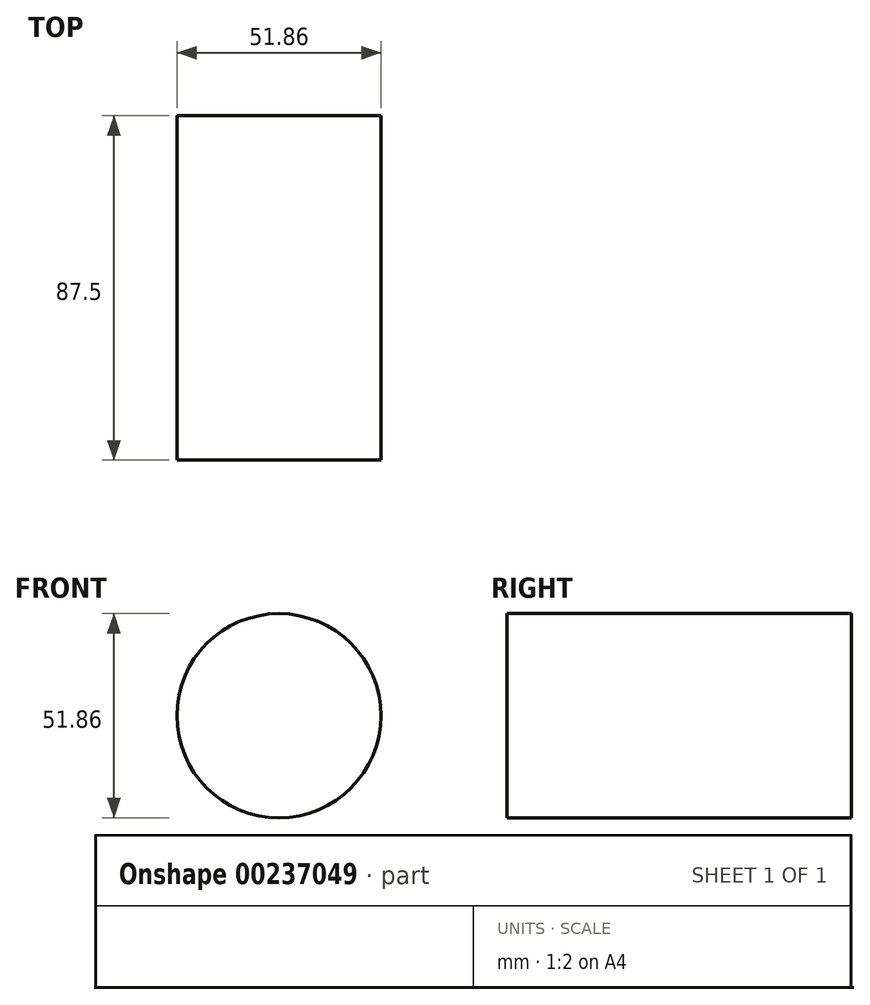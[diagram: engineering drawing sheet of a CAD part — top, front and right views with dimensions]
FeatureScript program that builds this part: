
annotation { "Feature Type Name" : "Feature", "Feature Type Description" : "" }
export const myFeature = defineFeature(function(context is Context, id is Id, definition is map)
    precondition{}
    {
        {
            var Q0;
            Q0=qCreatedBy(makeId("Front.planeOp"),FACE);
            var sketch = newSketch(context, id + "F0", { "sketchPlane" : qUnion([Q0])});
            skCircle(sketch, "E0", {"center": v(-28.26, 35.9) * mm, "radius": 25.93 * mm});
            skSolve(sketch);
        }
        {
            var Q0;
            Q0=makeQuery(id+"F0.imprint","IMPRINT",FACE,{"disambiguationData":[TD([[makeQuery(id+"F0.imprint","IMPRINT",EDGE,{"derivedFrom":sQuery(id+"F0.wireOp",EDGE,"E0")}),1.0]])]});
            extrude(context, id + "F1", {"entities" : qUnion([Q0]), "depth" : 87.5 * mm});
        }
    });
